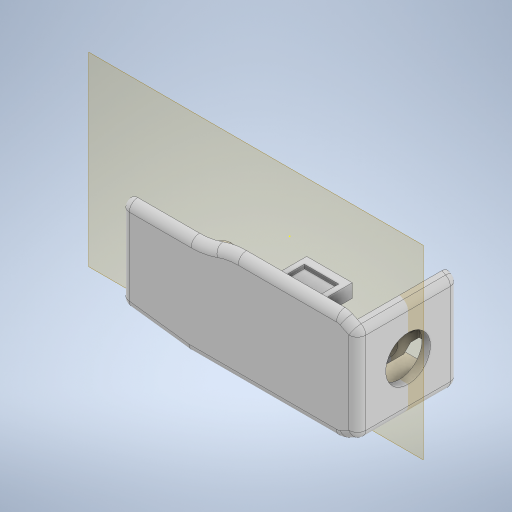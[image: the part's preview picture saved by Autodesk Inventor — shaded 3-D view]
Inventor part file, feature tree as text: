
AUTODESK INVENTOR PART (.ipt)
format: ipt  version: 2023 (Build 270158000, 158)  size: 614,400 bytes
history: native  units: in
note: dims shown in document units (in); Inventor stores cm internally (conversion verified against a paired STEP export)
features: sketch x25, extrude x24, fillet x10, plane x5, chamfer x3, mirror x2, projected_geometry x1
ambient origin geometry x8: Origin, YZ Plane, XZ Plane, XY Plane, X Axis, Y Axis, Z Axis, Center Point
bodies: Solid1 (feature_tree)
feature tree (70):
  extrude  "Extrusion1"  Depth=2.3622in
  sketch  "Sketch2"  dims[d2=2.3622in d3=0.0in d4=3.5433in d5=0.1969in d6=0.0in]
  extrude  "Extrusion2"  Depth=0.1969in
  chamfer  "Chamfer2"  Distance=0.1969in
  extrude  "Extrusion6"  Depth=1.5748in
  extrude  "Extrusion7"  Depth=1.1811in
  plane  "Work Plane1"
  fillet  "Fillet6"  Radius=0.3937in
  fillet  "Fillet9"  Radius=0.1969in
  fillet  "Fillet21"  Radius=0.1969in
  fillet  "Fillet22"  Radius=0.1969in
  chamfer  "Chamfer3"  Distance=2.1654in
  fillet  "Fillet23"  Radius=0.1969in
  fillet  "Fillet24"  Radius=0.1969in
  chamfer  "Chamfer4"  Distance=0.3937in Angle=45.0deg
  fillet  "Fillet25"  Radius=0.1969in
  fillet  "Fillet26"  Radius=0.3937in
  fillet  "Fillet27"  Radius=1.2795in
  plane  "Work Plane7"
  extrude  "Extrusion21"  Depth=0.3937in
  extrude  "Extrusion24"  Depth=0.1969in
  extrude  "Extrusion25"  TaperAngle=0.0deg  [1 undecoded]
  extrude  "Extrusion26"  Depth=0.1969in
  extrude  "Extrusion27"  Depth=0.3937in TaperAngle=0.0deg
  extrude  "Extrusion29"  Depth=0.3937in TaperAngle=0.0deg
  plane  "Work Plane4"
  extrude  "Extrusion30"  Depth=0.1181in
  extrude  "Extrusion31"  Depth=0.0984in
  extrude  "Extrusion32"  Depth=0.0984in
  extrude  "Extrusion33"  Depth=0.3937in TaperAngle=0.0deg
  plane  "Work Plane6"
  extrude  "Extrusion36"  Depth=1.7717in
  extrude  "Extrusion37"  Depth=0.2756in
  extrude  "Extrusion38"  Depth=0.7087in
  mirror  "Mirror1"
  extrude  "Extrusion39"  Depth=0.4724in TaperAngle=0.0deg
  mirror  "Mirror2"
  extrude  "Extrusion40"  Depth=0.1378in
  extrude  "Extrusion41"  Depth=0.1378in
  extrude  "Extrusion42"  Depth=0.1378in
  fillet  "Fillet29"  Radius=0.1969in
  extrude  "Extrusion43"  Depth=0.4724in TaperAngle=0.0deg
  extrude  "Extrusion44"  TaperAngle=0.0deg  [1 undecoded]
  extrude  "Extrusion45"  Depth=0.3937in TaperAngle=0.0deg
  sketch  "Sketch1"  dims[d0=5.5118in d1=2.3622in]
  sketch  "Sketch3"  dims[d10=0.1969in d11=1.5748in d12=45.0deg d26=1.0433in]
  sketch  "Sketch8"  dims[d27=1.2795in d28=1.1811in d29=0.3937in d30=0.0in d35=0.1969in d36=0.1969in d37=0.1969in]
  sketch  "Sketch9"  dims[d38=0.1969in]
  sketch  "Sketch24"  dims[d39=0.1969in]
  sketch  "Sketch27"  dims[d40=0.1969in]
  sketch  "Sketch28"  dims[d41=0.1969in d42=2.1654in d43=0.0in d66=0.1969in d69=0.1969in]
  sketch  "Sketch29"  dims[d81=1.5748in]
  sketch  "Sketch30"  dims[d82=1.5748in d83=0.3937in d84=0.1969in d85=45.0deg d86=0.1969in d87=0.3937in d88=1.2795in]
  sketch  "Sketch32"  dims[d89=0.1969in d90=0.3937in d91=45.0deg d92=0.3937in]
  sketch  "Sketch34"  dims[d93=0.1969in d94=0.1969in]
  sketch  "Sketch35"  dims[d129=0.1969in d130=0.0in d137=0.0in]
  sketch  "Sketch37"  dims[d138=0.748in d139=0.1969in]
  sketch  "Sketch38"  dims[d140=0.1969in d141=0.3937in d142=0.0in]
  projected_geometry  "Projected Loop4"
  plane  "Work Plane5"
  sketch  "Sketch42"  dims[d143=0.1969in d144=0.3937in d145=0.0in]
  sketch  "Sketch43"  dims[d146=0.1772in d147=0.1181in]
  sketch  "Sketch44"  dims[d148=0.0984in d149=0.0984in]
  sketch  "Sketch45"  dims[d150=0.3937in d151=0.0in d152=0.0984in]
  sketch  "Sketch46"  dims[d153=0.2756in d154=0.3937in d155=0.0in]
  sketch  "Sketch47"  dims[d158=1.122in d159=1.7717in]
  sketch  "Sketch48"  dims[d160=0.1969in d161=0.0in d163=0.2756in]
  sketch  "Sketch49"  dims[d164=0.2756in d166=0.7087in]
  sketch  "Sketch50"  dims[d167=1.4961in d168=0.4724in d169=0.0in]
  sketch  "Sketch51"  dims[d170=0.1575in d171=0.1378in d172=0.1378in d173=0.1378in d174=0.1969in d175=0.0in d176=0.4724in d177=0.0in d178=0.0in d179=0.3937in d180=0.0in d193=0.5906in d194=0.5118in d195=0.1969in d196=0.0in d197=0.4724in d199=0.3937in d200=0.0984in d201=0.0in d202=45.0deg d203=45.0deg d204=0.1969in d205=0.0in d206=45.0deg d207=45.0deg d208=0.1969in d209=0.0in d210=0.315in d211=0.1969in d212=0.0in d213=0.3937in d214=0.0in d215=0.3937in d216=0.0in d217=0.1965in d218=0.315in d219=0.1969in d220=0.4055in d221=0.7992in d222=0.0906in d223=0.0in d224=0.9055in d225=1.063in d226=0.2047in d227=0.315in d228=0.7874in d229=0.0in d230=0.1969in d231=0.4055in d232=0.7992in d233=0.1319in d234=0.1319in d235=0.0906in d236=0.0in d109=0.0197in d110=0.0344in d111=0.0197in d112=0.0344in d131=0.0197in d132=0.0344in d133=0.0197in d134=0.0344in]
note: 2 required parameter values undecoded (feature->parameter linkage not recoverable at this tier; creation-order binding heuristic only, values carry confidence <= 0.55)
